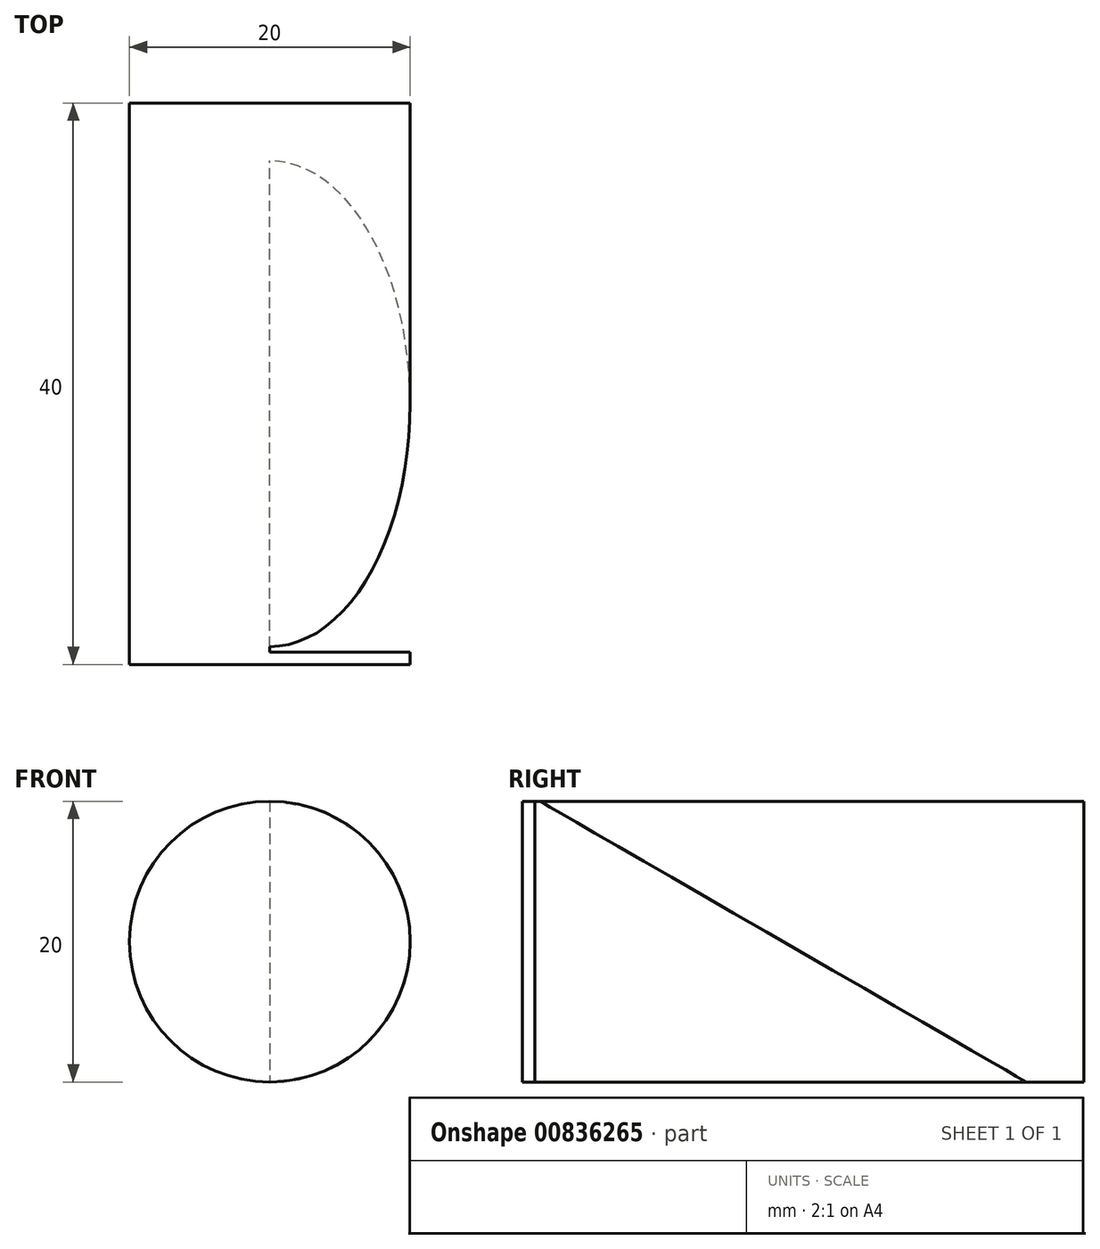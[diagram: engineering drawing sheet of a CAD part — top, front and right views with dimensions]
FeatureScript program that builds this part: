
annotation { "Feature Type Name" : "Feature", "Feature Type Description" : "" }
export const myFeature = defineFeature(function(context is Context, id is Id, definition is map)
    precondition{}
    {
        {
            var Q0;
            Q0=qCreatedBy(makeId("Front.planeOp"),FACE);
            var sketch = newSketch(context, id + "F0", { "sketchPlane" : qUnion([Q0])});
            skCircle(sketch, "E0", {"center": v(0, 0) * mm, "radius": 10 * mm});
            skSolve(sketch);
        }
        {
            var Q0;
            Q0=makeQuery(id+"F0.imprint","IMPRINT",FACE,{"disambiguationData":[TD([[makeQuery(id+"F0.imprint","IMPRINT",EDGE,{"derivedFrom":sQuery(id+"F0.wireOp",EDGE,"E0")}),1.0]])]});
            extrude(context, id + "F1", {"entities" : qUnion([Q0]), "depth" : 40 * mm, "offsetDistance" : 25 * mm});
        }
        {
            var Q0;
            Q0=makeQuery(id+"F1.opExtrude","CAP_FACE",FACE,{"disambiguationData":[OSD([sQuery(id+"F0.wireOp",EDGE,"E0")])],"isStart":false});
            var sketch = newSketch(context, id + "F2", { "sketchPlane" : qUnion([Q0])});
            skLineSegment(sketch, "E1", {"start": v(-17.8, 0) * mm, "end": v(16.77, 0) * mm});
            skSolve(sketch);
        }
        {
            var Q0;
            Q0=qCreatedBy(makeId("Right.planeOp"),FACE);
            var sketch = newSketch(context, id + "F3", { "sketchPlane" : qUnion([Q0])});
            skLineSegment(sketch, "E2", {"start": v(-116.4, 34.74) * mm, "end": v(-96.58, 0) * mm});
            skLineSegment(sketch, "E3", {"start": v(-39.13, 10.22) * mm, "end": v(-3.34, -10.45) * mm});
            skLineSegment(sketch, "E4", {"start": v(-39.13, 14.97) * mm, "end": v(-39.13, -15.08) * mm});
            skLineSegment(sketch, "E5", {"start": v(-3.34, -10.45) * mm, "end": v(-45.4, -10.45) * mm});
            skSolve(sketch);
        }
        {
            var Q0;
            Q0 = qSketchRegion(id + "F3", true);
            extrude(context, id + "F4", {"entities" : qUnion([Q0]), "operationType" : NewBodyOperationType.REMOVE, "depth" : 80 * mm, "offsetDistance" : 25 * mm});
        }
    });
